# Revit family: LWP2LIFE-PRO-WPPOD-HV
name_source: partatom
category: Lighting Fixtures
units: mm (PartAtom-declared; Revit-internal decimal feet)

## family parameters
Cut with Voids When Loaded = No
Host = Face
Light Source = Yes
OmniClass Number = 23.80.70.11.21
OmniClass Title = Emergency Lighting
Part Type = Normal
Room Calculation Point = No
Round Connector Dimension = Use Diameter
Shared = No

## types (1)
- LWP2LIFE-PRO-WPPOD-HV
    Clevertronics_AS2293 Classification = C0=D160 C90=D160
    Clevertronics_Battery = 3.3V 2500mAh
    Clevertronics_Battery Type = Lithium Nanophosphate
    Clevertronics_Charger Method = Intelligent current limited constant voltage
    Clevertronics_Construction = Polycarbonate
    Clevertronics_Dimensions Main Enclosure = 520mm x 180mm x 135mm
    Clevertronics_IP Rating = IP65
    Clevertronics_MIC Number = AUT01820080001
    Clevertronics_Mounting = Surface mount
    Clevertronics_Operating Mode = Non-maintained
    Clevertronics_Operating Temperature = 0˚C to 40˚C
    Clevertronics_Operating Voltage = 240V AC; 50Hz
    Clevertronics_Part Number = LWP2LIFE-PRO-WPPOD-HV
    Clevertronics_Power Consumption = 0.8 Watts (Standby), 5.5 Watts (Max)
    Clevertronics_Product Description = L10 Lithium Nanophosphate Lifelight Pro, high performance, IP65 surface mounted 
Emergency Light with twin rotatable LED Pods
    Clevertronics_Replacement Battery = 1530050:Battery, L10 3.3V 2500mAh 70mm lead, no Bracket
    Clevertronics_Replacement Lamp = 2750353
    Clevertronics_Testing System = Zoneworks XT HIVE (RF)
    Clevertronics_Weight = 3.4kg
    Color Filter = 16777215
    Default Elevation = 2100 mm
    Description = L10 Lithium Nanophosphate Lifelight Pro, high performance, IP65 surface mounted 
Emergency Light with twin rotatable LED Pods
rotatable LED Pods
    Dimming Lamp Color Temperature Shift = <None>
    Indication Left = Yes
    Indication Left 'Face Two' = No
    Indication Left 'Face one' = Yes
    Indication Right = No
    Indication Right 'Face one' = No
    Lamp = Twin Dual LED (Lifetime warranty on the lamp head and loom assembly)
    Manufacturer = Clevertronics
    Material = Clevertronics_White
    Photometric Web File = CWP2LIFE-PRO-WPPOD_IESR_E_669-3_20180810.ies
    Runing Man common arrow = No
    Straight line = No
    Straight line 'Face one' = No
    Straight line 'Face two' = No
    Tilt Angle = -60.00°

## geometry (parser evidence)
native form markers: Sweep x6
no freeform markers — native parametric forms only
